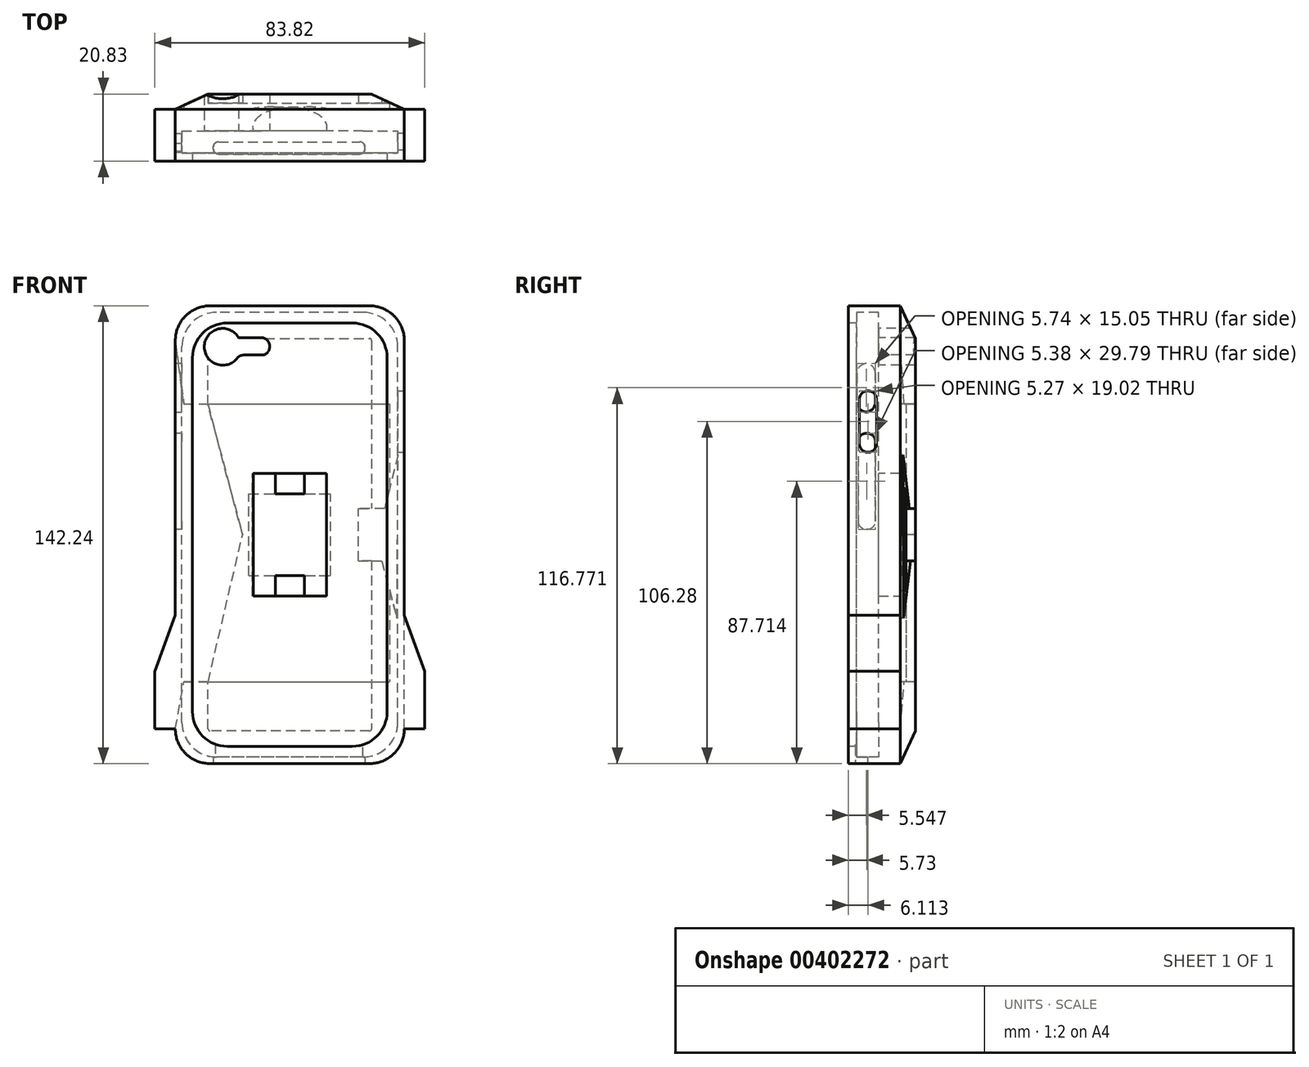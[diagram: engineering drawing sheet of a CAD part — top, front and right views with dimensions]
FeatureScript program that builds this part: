
annotation { "Feature Type Name" : "Feature", "Feature Type Description" : "" }
export const myFeature = defineFeature(function(context is Context, id is Id, definition is map)
    precondition{}
    {
        {
            var Q0;
            Q0=qCreatedBy(makeId("Front.planeOp"),FACE);
            var sketch = newSketch(context, id + "F0", { "sketchPlane" : qUnion([Q0])});
            skLineSegment(sketch, "E0.bottom", {"start": v(33.53, -69.09) * mm, "end": v(-33.53, -69.09) * mm});
            skLineSegment(sketch, "E0.top", {"start": v(33.53, 69.09) * mm, "end": v(-33.53, 69.09) * mm});
            skLineSegment(sketch, "E0.left", {"start": v(33.53, -69.09) * mm, "end": v(33.53, 69.09) * mm});
            skLineSegment(sketch, "E0.right", {"start": v(-33.53, -69.09) * mm, "end": v(-33.53, 69.09) * mm});
            skPoint(sketch, "E0.middle", {"position": v(0, 0) * mm});
            skSolve(sketch);
        }
        {
            var Q0;
            Q0=qCreatedBy(makeId("Front.planeOp"),FACE);
            var sketch = newSketch(context, id + "F1", { "sketchPlane" : qUnion([Q0])});
            skLineSegment(sketch, "E1.bottom", {"start": v(35.56, -71.12) * mm, "end": v(-35.56, -71.12) * mm});
            skLineSegment(sketch, "E1.top", {"start": v(35.56, 71.12) * mm, "end": v(-35.56, 71.12) * mm});
            skLineSegment(sketch, "E1.left", {"start": v(35.56, -71.12) * mm, "end": v(35.56, 71.12) * mm});
            skLineSegment(sketch, "E1.right", {"start": v(-35.56, -71.12) * mm, "end": v(-35.56, 71.12) * mm});
            skPoint(sketch, "E1.middle", {"position": v(0, 0) * mm});
            skSolve(sketch);
        }
        {
            var Q0;
            Q0=makeQuery(id+"F1.imprint","IMPRINT",FACE,{"disambiguationData":[TD([[makeQuery(id+"F1.imprint","IMPRINT",EDGE,{"derivedFrom":sQuery(id+"F1.wireOp",EDGE,"E1.bottom")}),-1.0]])]});
            extrude(context, id + "F2", {"entities" : qUnion([Q0]), "oppositeDirection" : true, "depth" : 11.94 * mm});
        }
        {
            var Q0;
            Q0=makeQuery(id+"F0.imprint","IMPRINT",FACE,{"disambiguationData":[TD([[makeQuery(id+"F0.imprint","IMPRINT",EDGE,{"derivedFrom":sQuery(id+"F0.wireOp",EDGE,"E0.bottom")}),-1.0]])]});
            extrude(context, id + "F3", {"entities" : qUnion([Q0]), "operationType" : NewBodyOperationType.REMOVE, "oppositeDirection" : true, "depth" : 9.4 * mm});
        }
        {
            var Q0;
            Q0=makeQuery(id+"F3.boolean.opBoolean","COPY",EDGE,{"derivedFrom":makeQuery(id+"F3.opExtrude","SWEPT_EDGE",EDGE,{"disambiguationData":[OSD([sQuery(id+"F0.wireOp",EDGE,"E0.top"),sQuery(id+"F0.wireOp",EDGE,"E0.right")])]})});
            var Q1;
            Q1=makeQuery(id+"F3.boolean.opBoolean","COPY",EDGE,{"derivedFrom":makeQuery(id+"F3.opExtrude","SWEPT_EDGE",EDGE,{"disambiguationData":[OSD([sQuery(id+"F0.wireOp",EDGE,"E0.top"),sQuery(id+"F0.wireOp",EDGE,"E0.left")])]})});
            var Q2;
            Q2=makeQuery(id+"F3.boolean.opBoolean","COPY",EDGE,{"derivedFrom":makeQuery(id+"F3.opExtrude","SWEPT_EDGE",EDGE,{"disambiguationData":[OSD([sQuery(id+"F0.wireOp",EDGE,"E0.bottom"),sQuery(id+"F0.wireOp",EDGE,"E0.left")])]})});
            var Q3;
            Q3=makeQuery(id+"F3.boolean.opBoolean","COPY",EDGE,{"derivedFrom":makeQuery(id+"F3.opExtrude","SWEPT_EDGE",EDGE,{"disambiguationData":[OSD([sQuery(id+"F0.wireOp",EDGE,"E0.bottom"),sQuery(id+"F0.wireOp",EDGE,"E0.right")])]})});
            fillet(context, id + "F4", {"entities" : qUnion([Q0, Q1, Q2, Q3]), "radius" : 10.8 * mm, "tangentPropagation" : true, "allowEdgeOverflow" : false});
        }
        {
            var Q0;
            Q0=makeQuery(id+"F2.opExtrude","SWEPT_EDGE",EDGE,{"disambiguationData":[OSD([sQuery(id+"F1.wireOp",EDGE,"E1.top"),sQuery(id+"F1.wireOp",EDGE,"E1.left")])]});
            var Q1;
            Q1=makeQuery(id+"F2.opExtrude","SWEPT_EDGE",EDGE,{"disambiguationData":[OSD([sQuery(id+"F1.wireOp",EDGE,"E1.top"),sQuery(id+"F1.wireOp",EDGE,"E1.right")])]});
            var Q2;
            Q2=makeQuery(id+"F2.opExtrude","SWEPT_EDGE",EDGE,{"disambiguationData":[OSD([sQuery(id+"F1.wireOp",EDGE,"E1.bottom"),sQuery(id+"F1.wireOp",EDGE,"E1.right")])]});
            var Q3;
            Q3=makeQuery(id+"F2.opExtrude","SWEPT_EDGE",EDGE,{"disambiguationData":[OSD([sQuery(id+"F1.wireOp",EDGE,"E1.bottom"),sQuery(id+"F1.wireOp",EDGE,"E1.left")])]});
            fillet(context, id + "F5", {"entities" : qUnion([Q0, Q1, Q2, Q3]), "radius" : 10.8 * mm, "tangentPropagation" : true, "allowEdgeOverflow" : false});
        }
        {
            var Q0;
            Q0=qCreatedBy(makeId("Right.planeOp"),FACE);
            var sketch = newSketch(context, id + "F6", { "sketchPlane" : qUnion([Q0])});
            skLineSegment(sketch, "E2.bottom", {"start": v(17.97, 40.7) * mm, "end": v(16.06, 40.7) * mm});
            skLineSegment(sketch, "E2.top", {"start": v(17.97, -45.67) * mm, "end": v(16.06, -45.67) * mm});
            skLineSegment(sketch, "E2.left", {"start": v(17.97, 40.7) * mm, "end": v(17.97, -45.67) * mm});
            skLineSegment(sketch, "E2.right", {"start": v(16.06, 40.7) * mm, "end": v(16.06, -45.67) * mm});
            skSolve(sketch);
        }
        {
            var Q0;
            Q0=qCreatedBy(makeId("Front.planeOp"),FACE);
            var sketch = newSketch(context, id + "F7", { "sketchPlane" : qUnion([Q0])});
            skLineSegment(sketch, "E3.bottom", {"start": v(33.53, -69.09) * mm, "end": v(-33.53, -69.09) * mm});
            skLineSegment(sketch, "E3.top", {"start": v(33.53, 69.09) * mm, "end": v(-33.53, 69.09) * mm});
            skLineSegment(sketch, "E3.left", {"start": v(33.53, -69.09) * mm, "end": v(33.53, 69.09) * mm});
            skLineSegment(sketch, "E3.right", {"start": v(-33.53, -69.09) * mm, "end": v(-33.53, 69.09) * mm});
            skPoint(sketch, "E3.middle", {"position": v(0, 0) * mm});
            skSolve(sketch);
        }
        {
            var Q0;
            Q0=qSketchRegion(id+"F7",true);
            extrude(context, id + "F8", {"entities" : qUnion([Q0]), "operationType" : NewBodyOperationType.ADD, "oppositeDirection" : true, "depth" : 2.54 * mm});
        }
        {
            var Q0;
            Q0=makeQuery(id+"F8.opExtrude","SWEPT_EDGE",EDGE,{"disambiguationData":[OSD([sQuery(id+"F7.wireOp",EDGE,"E3.top"),sQuery(id+"F7.wireOp",EDGE,"E3.right")])]});
            var Q1;
            Q1=makeQuery(id+"F8.opExtrude","SWEPT_EDGE",EDGE,{"disambiguationData":[OSD([sQuery(id+"F7.wireOp",EDGE,"E3.top"),sQuery(id+"F7.wireOp",EDGE,"E3.left")])]});
            var Q2;
            Q2=makeQuery(id+"F8.opExtrude","SWEPT_EDGE",EDGE,{"disambiguationData":[OSD([sQuery(id+"F7.wireOp",EDGE,"E3.bottom"),sQuery(id+"F7.wireOp",EDGE,"E3.left")])]});
            var Q3;
            Q3=makeQuery(id+"F8.opExtrude","SWEPT_EDGE",EDGE,{"disambiguationData":[OSD([sQuery(id+"F7.wireOp",EDGE,"E3.bottom"),sQuery(id+"F7.wireOp",EDGE,"E3.right")])]});
            fillet(context, id + "F9", {"entities" : qUnion([Q0, Q1, Q2, Q3]), "radius" : 10.8 * mm, "tangentPropagation" : true, "allowEdgeOverflow" : false});
        }
        {
            var Q0;
            Q0=qCreatedBy(makeId("Front.planeOp"),FACE);
            var sketch = newSketch(context, id + "F10", { "sketchPlane" : qUnion([Q0])});
            skLineSegment(sketch, "E4.bottom", {"start": v(30.23, -65.79) * mm, "end": v(-30.23, -65.79) * mm});
            skLineSegment(sketch, "E4.top", {"start": v(30.23, 65.79) * mm, "end": v(-30.23, 65.79) * mm});
            skLineSegment(sketch, "E4.left", {"start": v(30.23, -65.79) * mm, "end": v(30.23, 65.79) * mm});
            skLineSegment(sketch, "E4.right", {"start": v(-30.23, -65.79) * mm, "end": v(-30.23, 65.79) * mm});
            skPoint(sketch, "E4.middle", {"position": v(0, 0) * mm});
            skSolve(sketch);
        }
        {
            var Q0;
            Q0=makeQuery(id+"F10.imprint","IMPRINT",FACE,{"disambiguationData":[TD([[makeQuery(id+"F10.imprint","IMPRINT",EDGE,{"derivedFrom":sQuery(id+"F10.wireOp",EDGE,"E4.bottom")}),-1.0]])]});
            extrude(context, id + "F11", {"entities" : qUnion([Q0]), "operationType" : NewBodyOperationType.REMOVE, "oppositeDirection" : true, "depth" : 2.8 * mm});
        }
        {
            var Q0;
            Q0=makeQuery(id+"F11.boolean.opBoolean","COPY",EDGE,{"derivedFrom":makeQuery(id+"F11.opExtrude","SWEPT_EDGE",EDGE,{"disambiguationData":[OSD([sQuery(id+"F10.wireOp",EDGE,"E4.top"),sQuery(id+"F10.wireOp",EDGE,"E4.right")])]})});
            var Q1;
            Q1=makeQuery(id+"F11.boolean.opBoolean","COPY",EDGE,{"derivedFrom":makeQuery(id+"F11.opExtrude","SWEPT_EDGE",EDGE,{"disambiguationData":[OSD([sQuery(id+"F10.wireOp",EDGE,"E4.top"),sQuery(id+"F10.wireOp",EDGE,"E4.left")])]})});
            var Q2;
            Q2=makeQuery(id+"F11.boolean.opBoolean","COPY",EDGE,{"derivedFrom":makeQuery(id+"F11.opExtrude","SWEPT_EDGE",EDGE,{"disambiguationData":[OSD([sQuery(id+"F10.wireOp",EDGE,"E4.bottom"),sQuery(id+"F10.wireOp",EDGE,"E4.left")])]})});
            var Q3;
            Q3=makeQuery(id+"F11.boolean.opBoolean","COPY",EDGE,{"derivedFrom":makeQuery(id+"F11.opExtrude","SWEPT_EDGE",EDGE,{"disambiguationData":[OSD([sQuery(id+"F10.wireOp",EDGE,"E4.bottom"),sQuery(id+"F10.wireOp",EDGE,"E4.right")])]})});
            fillet(context, id + "F12", {"entities" : qUnion([Q0, Q1, Q2, Q3]), "radius" : 10.8 * mm, "tangentPropagation" : true, "allowEdgeOverflow" : false});
        }
        {
            var Q0;
            Q0=qCreatedBy(makeId("Right.planeOp"),FACE);
            var sketch = newSketch(context, id + "F13", { "sketchPlane" : qUnion([Q0])});
            skCircle(sketch, "E5", {"center": v(16.23, -1.76) * mm, "radius": 3.17 * mm});
            skSolve(sketch);
        }
        {
            var Q0;
            Q0=qSketchRegion(id+"F13",true);
            extrude(context, id + "F14", {"entities" : qUnion([Q0]), "operationType" : NewBodyOperationType.REMOVE, "endBound" : BoundingType.SYMMETRIC, "oppositeDirection" : true, "depth" : 101.6 * mm});
        }
        {
            var Q0;
            Q0=makeQuery(id+"F2.opExtrude","CAP_FACE",FACE,{"disambiguationData":[OSD([sQuery(id+"F1.wireOp",EDGE,"E1.bottom"),sQuery(id+"F1.wireOp",EDGE,"E1.top"),sQuery(id+"F1.wireOp",EDGE,"E1.left"),sQuery(id+"F1.wireOp",EDGE,"E1.right")])],"isStart":false});
            var sketch = newSketch(context, id + "F15", { "sketchPlane" : qUnion([Q0])});
            skLineSegment(sketch, "E6.bottom", {"start": v(35.56, -71.12) * mm, "end": v(-35.56, -71.12) * mm});
            skLineSegment(sketch, "E6.top", {"start": v(35.56, 71.12) * mm, "end": v(-35.56, 71.12) * mm});
            skLineSegment(sketch, "E6.left", {"start": v(35.56, -71.12) * mm, "end": v(35.56, 71.12) * mm});
            skLineSegment(sketch, "E6.right", {"start": v(-35.56, -71.12) * mm, "end": v(-35.56, 71.12) * mm});
            skPoint(sketch, "E6.middle", {"position": v(0, 0) * mm});
            skSolve(sketch);
        }
        {
            var Q0;
            Q0 = qSketchRegion(id + "F15", true);
            extrude(context, id + "F16", {"entities" : qUnion([Q0]), "operationType" : NewBodyOperationType.ADD, "depth" : 8.9 * mm});
        }
        {
            var Q0;
            Q0=makeQuery(id+"F16.opExtrude","SWEPT_EDGE",EDGE,{"disambiguationData":[OSD([sQuery(id+"F15.wireOp",EDGE,"E6.top"),sQuery(id+"F15.wireOp",EDGE,"E6.left")])]});
            var Q1;
            Q1=makeQuery(id+"F16.opExtrude","SWEPT_EDGE",EDGE,{"disambiguationData":[OSD([sQuery(id+"F15.wireOp",EDGE,"E6.top"),sQuery(id+"F15.wireOp",EDGE,"E6.right")])]});
            var Q2;
            Q2=makeQuery(id+"F16.opExtrude","SWEPT_EDGE",EDGE,{"disambiguationData":[OSD([sQuery(id+"F15.wireOp",EDGE,"E6.bottom"),sQuery(id+"F15.wireOp",EDGE,"E6.right")])]});
            var Q3;
            Q3=makeQuery(id+"F16.opExtrude","SWEPT_EDGE",EDGE,{"disambiguationData":[OSD([sQuery(id+"F15.wireOp",EDGE,"E6.bottom"),sQuery(id+"F15.wireOp",EDGE,"E6.left")])]});
            fillet(context, id + "F17", {"entities" : qUnion([Q0, Q1, Q2, Q3]), "radius" : 10.8 * mm, "tangentPropagation" : true, "allowEdgeOverflow" : false});
        }
        {
            var Q0;
            Q0 = qSketchRegion(id + "F6", true);
            extrude(context, id + "F18", {"entities" : qUnion([Q0]), "operationType" : NewBodyOperationType.REMOVE, "oppositeDirection" : true, "depth" : 45.97 * mm});
        }
        {
            var Q0;
            Q0=makeQuery(id+"F16.opExtrude","CAP_EDGE",EDGE,{"disambiguationData":[OSD([sQuery(id+"F15.wireOp",EDGE,"E6.left")])],"isStart":false});
            var Q1;
            Q1=makeQuery(id+"F16.opExtrude","CAP_EDGE",EDGE,{"disambiguationData":[OSD([sQuery(id+"F15.wireOp",EDGE,"E6.right")])],"isStart":false});
            chamfer(context, id + "F19", {"entities" : qUnion([Q0, Q1]), "chamferType" : ChamferType.OFFSET_ANGLE, "width" : 10.16 * mm, "oppositeDirection" : false, "angle" : 25 * degree, "tangentPropagation" : true});
        }
        {
            var Q0;
            Q0=makeQuery(id+"F18.boolean.opBoolean","COPY",FACE,{"derivedFrom":makeQuery(id+"F18.opExtrude","SWEPT_FACE",FACE,{"disambiguationData":[OSD([sQuery(id+"F6.wireOp",EDGE,"E2.right")])]})});
            var sketch = newSketch(context, id + "F20", { "sketchPlane" : qUnion([Q0])});
            skLineSegment(sketch, "E7", {"start": v(35.56, 60.36) * mm, "end": v(32.88, 40.7) * mm});
            skLineSegment(sketch, "E8", {"start": v(32.88, 40.7) * mm, "end": v(25.49, 40.7) * mm});
            skLineSegment(sketch, "E9", {"start": v(25.49, 40.7) * mm, "end": v(14.68, 0) * mm});
            skLineSegment(sketch, "E10", {"start": v(14.68, 0) * mm, "end": v(25.36, -45.67) * mm});
            skLineSegment(sketch, "E11", {"start": v(25.36, -45.67) * mm, "end": v(32.88, -45.67) * mm});
            skLineSegment(sketch, "E12", {"start": v(32.88, -45.67) * mm, "end": v(35.56, -60.32) * mm});
            skLineSegment(sketch, "E13", {"start": v(35.56, -60.32) * mm, "end": v(35.56, 60.36) * mm});
            skSolve(sketch);
        }
        {
            var Q0;
            Q0 = qSketchRegion(id + "F20", true);
            extrude(context, id + "F21", {"entities" : qUnion([Q0]), "operationType" : NewBodyOperationType.REMOVE, "depth" : 45.47 * mm});
        }
        {
            var Q0;
            Q0=makeQuery(id+"F21.boolean.opBoolean","MERGE",FACE,{"derivedFrom":[makeQuery(id+"F18.boolean.opBoolean","COPY",FACE,{"derivedFrom":makeQuery(id+"F18.opExtrude","SWEPT_FACE",FACE,{"disambiguationData":[OSD([sQuery(id+"F6.wireOp",EDGE,"E2.right")])]})}),makeQuery(id+"F21.opExtrude","CAP_FACE",FACE,{"disambiguationData":[OSD([sQuery(id+"F20.wireOp",EDGE,"E7"),sQuery(id+"F20.wireOp",EDGE,"E8"),sQuery(id+"F20.wireOp",EDGE,"E9"),sQuery(id+"F20.wireOp",EDGE,"E10"),sQuery(id+"F20.wireOp",EDGE,"E11"),sQuery(id+"F20.wireOp",EDGE,"E12"),sQuery(id+"F20.wireOp",EDGE,"E13")])],"isStart":true})]});
            var sketch = newSketch(context, id + "F22", { "sketchPlane" : qUnion([Q0])});
            skLineSegment(sketch, "E14", {"start": v(-33.6, 24.75) * mm, "end": v(-29.43, 8.07) * mm});
            skLineSegment(sketch, "E15", {"start": v(-29.43, 8.07) * mm, "end": v(-21.34, 8.07) * mm});
            skLineSegment(sketch, "E16", {"start": v(-21.34, 8.07) * mm, "end": v(-21.34, -8.12) * mm});
            skLineSegment(sketch, "E17", {"start": v(-21.34, -8.12) * mm, "end": v(-28.55, -8.12) * mm});
            skLineSegment(sketch, "E18", {"start": v(-28.55, -8.12) * mm, "end": v(-33.26, -25.98) * mm});
            skLineSegment(sketch, "E19", {"start": v(-33.26, -25.98) * mm, "end": v(-33.6, 24.75) * mm});
            skSolve(sketch);
        }
        {
            var Q0;
            Q0 = qSketchRegion(id + "F22", true);
            extrude(context, id + "F23", {"entities" : qUnion([Q0]), "operationType" : NewBodyOperationType.REMOVE, "depth" : 84.58 * mm});
        }
        {
            var Q0;
            Q0 = qSketchRegion(id + "F6", true);
            extrude(context, id + "F24", {"entities" : qUnion([Q0]), "operationType" : NewBodyOperationType.REMOVE, "depth" : 30.99 * mm});
        }
        {
            var Q0;
            Q0=makeQuery(id+"F16.boolean.opBoolean","MERGE",FACE,{"derivedFrom":[makeQuery(id+"F2.opExtrude","SWEPT_FACE",FACE,{"disambiguationData":[OSD([sQuery(id+"F1.wireOp",EDGE,"E1.left")])]}),makeQuery(id+"F16.opExtrude","SWEPT_FACE",FACE,{"disambiguationData":[OSD([sQuery(id+"F15.wireOp",EDGE,"E6.right")])]})]});
            var sketch = newSketch(context, id + "F25", { "sketchPlane" : qUnion([Q0])});
            skLineSegment(sketch, "E20.bottom", {"start": v(3.48, 44.67) * mm, "end": v(8.75, 44.67) * mm});
            skLineSegment(sketch, "E20.top", {"start": v(3.48, 25.65) * mm, "end": v(8.75, 25.65) * mm});
            skLineSegment(sketch, "E20.left", {"start": v(3.48, 44.67) * mm, "end": v(3.48, 25.65) * mm});
            skLineSegment(sketch, "E20.right", {"start": v(8.75, 44.67) * mm, "end": v(8.75, 25.65) * mm});
            skSolve(sketch);
        }
        {
            var Q0;
            Q0=makeQuery(id+"F25.imprint","IMPRINT",FACE,{"disambiguationData":[TD([[makeQuery(id+"F25.imprint","IMPRINT",EDGE,{"derivedFrom":sQuery(id+"F25.wireOp",EDGE,"E20.bottom")}),-1.0]])]});
            extrude(context, id + "F26", {"entities" : qUnion([Q0]), "operationType" : NewBodyOperationType.REMOVE, "oppositeDirection" : true, "depth" : 9.65 * mm});
        }
        {
            var Q0;
            Q0=makeQuery(id+"F26.boolean.opBoolean","COPY",EDGE,{"derivedFrom":makeQuery(id+"F26.opExtrude","SWEPT_EDGE",EDGE,{"disambiguationData":[OSD([sQuery(id+"F25.wireOp",EDGE,"E20.bottom"),sQuery(id+"F25.wireOp",EDGE,"E20.right")])]})});
            var Q1;
            Q1=makeQuery(id+"F26.boolean.opBoolean","COPY",EDGE,{"derivedFrom":makeQuery(id+"F26.opExtrude","SWEPT_EDGE",EDGE,{"disambiguationData":[OSD([sQuery(id+"F25.wireOp",EDGE,"E20.bottom"),sQuery(id+"F25.wireOp",EDGE,"E20.left")])]})});
            var Q2;
            Q2=makeQuery(id+"F26.boolean.opBoolean","COPY",EDGE,{"derivedFrom":makeQuery(id+"F26.opExtrude","SWEPT_EDGE",EDGE,{"disambiguationData":[OSD([sQuery(id+"F25.wireOp",EDGE,"E20.top"),sQuery(id+"F25.wireOp",EDGE,"E20.right")])]})});
            var Q3;
            Q3=makeQuery(id+"F26.boolean.opBoolean","COPY",EDGE,{"derivedFrom":makeQuery(id+"F26.opExtrude","SWEPT_EDGE",EDGE,{"disambiguationData":[OSD([sQuery(id+"F25.wireOp",EDGE,"E20.top"),sQuery(id+"F25.wireOp",EDGE,"E20.left")])]})});
            fillet(context, id + "F27", {"entities" : qUnion([Q0, Q1, Q2, Q3]), "radius" : 2.45 * mm, "tangentPropagation" : true, "allowEdgeOverflow" : false});
        }
        {
            var Q0;
            Q0=makeQuery(id+"F3.boolean.opBoolean","COPY",FACE,{"derivedFrom":makeQuery(id+"F3.opExtrude","CAP_FACE",FACE,{"disambiguationData":[OSD([sQuery(id+"F0.wireOp",EDGE,"E0.bottom"),sQuery(id+"F0.wireOp",EDGE,"E0.top"),sQuery(id+"F0.wireOp",EDGE,"E0.left"),sQuery(id+"F0.wireOp",EDGE,"E0.right")])],"isStart":false})});
            var sketch = newSketch(context, id + "F28", { "sketchPlane" : qUnion([Q0])});
            skCircle(sketch, "E21", {"center": v(-20.85, 58.37) * mm, "radius": 5.72 * mm});
            skSolve(sketch);
        }
        {
            var Q0;
            Q0=makeQuery(id+"F28.imprint","IMPRINT",FACE,{"disambiguationData":[TD([[makeQuery(id+"F28.imprint","IMPRINT",EDGE,{"derivedFrom":sQuery(id+"F28.wireOp",EDGE,"E21")}),1.0]])]});
            extrude(context, id + "F29", {"entities" : qUnion([Q0]), "operationType" : NewBodyOperationType.REMOVE, "oppositeDirection" : true, "depth" : 25.4 * mm});
        }
        {
            var Q0;
            Q0=makeQuery(id+"F3.boolean.opBoolean","COPY",FACE,{"derivedFrom":makeQuery(id+"F3.opExtrude","CAP_FACE",FACE,{"disambiguationData":[OSD([sQuery(id+"F0.wireOp",EDGE,"E0.bottom"),sQuery(id+"F0.wireOp",EDGE,"E0.top"),sQuery(id+"F0.wireOp",EDGE,"E0.left"),sQuery(id+"F0.wireOp",EDGE,"E0.right")])],"isStart":false})});
            var sketch = newSketch(context, id + "F30", { "sketchPlane" : qUnion([Q0])});
            skLineSegment(sketch, "E22.bottom", {"start": v(-20.56, 55.8) * mm, "end": v(-6.28, 55.8) * mm});
            skLineSegment(sketch, "E22.top", {"start": v(-20.56, 61.2) * mm, "end": v(-6.28, 61.2) * mm});
            skLineSegment(sketch, "E22.left", {"start": v(-20.56, 55.8) * mm, "end": v(-20.56, 61.2) * mm});
            skLineSegment(sketch, "E22.right", {"start": v(-6.28, 55.8) * mm, "end": v(-6.28, 61.2) * mm});
            skSolve(sketch);
        }
        {
            var Q0;
            Q0 = qSketchRegion(id + "F30", true);
            extrude(context, id + "F31", {"entities" : qUnion([Q0]), "operationType" : NewBodyOperationType.REMOVE, "oppositeDirection" : true, "depth" : 25.4 * mm});
        }
        {
            var Q0;
            Q0=makeQuery(id+"F31.boolean.opBoolean","COPY",EDGE,{"derivedFrom":makeQuery(id+"F31.opExtrude","SWEPT_EDGE",EDGE,{"disambiguationData":[OSD([sQuery(id+"F30.wireOp",EDGE,"E22.top"),sQuery(id+"F30.wireOp",EDGE,"E22.right")])]})});
            var Q1;
            Q1=makeQuery(id+"F31.boolean.opBoolean","COPY",EDGE,{"derivedFrom":makeQuery(id+"F31.opExtrude","SWEPT_EDGE",EDGE,{"disambiguationData":[OSD([sQuery(id+"F30.wireOp",EDGE,"E22.bottom"),sQuery(id+"F30.wireOp",EDGE,"E22.right")])]})});
            var Q2;
            Q2=makeQuery(id+"F31.boolean.opBoolean","INTERSECT",EDGE,{"derivedFrom":[makeQuery(id+"F29.boolean.opBoolean","COPY",FACE,{"derivedFrom":makeQuery(id+"F29.opExtrude","SWEPT_FACE",FACE,{"disambiguationData":[OSD([sQuery(id+"F28.wireOp",EDGE,"E21")])]})}),makeQuery(id+"F31.opExtrude","SWEPT_FACE",FACE,{"disambiguationData":[OSD([sQuery(id+"F30.wireOp",EDGE,"E22.bottom")])]})]});
            fillet(context, id + "F32", {"entities" : qUnion([Q0, Q1, Q2]), "radius" : 2.47 * mm, "tangentPropagation" : true, "allowEdgeOverflow" : false});
        }
        {
            var Q0;
            {var subQ0=sQuery(id+"F6.wireOp",EDGE,"E2.right");Q0=makeQuery(id+"F24.boolean.opBoolean","MERGE",FACE,{"derivedFrom":[makeQuery(id+"F21.boolean.opBoolean","MERGE",FACE,{"derivedFrom":[makeQuery(id+"F18.boolean.opBoolean","COPY",FACE,{"derivedFrom":makeQuery(id+"F18.opExtrude","SWEPT_FACE",FACE,{"disambiguationData":[OSD([subQ0])]})}),makeQuery(id+"F21.opExtrude","CAP_FACE",FACE,{"disambiguationData":[OSD([sQuery(id+"F20.wireOp",EDGE,"E7"),sQuery(id+"F20.wireOp",EDGE,"E8"),sQuery(id+"F20.wireOp",EDGE,"E9"),sQuery(id+"F20.wireOp",EDGE,"E10"),sQuery(id+"F20.wireOp",EDGE,"E11"),sQuery(id+"F20.wireOp",EDGE,"E12"),sQuery(id+"F20.wireOp",EDGE,"E13")])],"isStart":true})]}),makeQuery(id+"F23.boolean.opBoolean","COPY",FACE,{"derivedFrom":makeQuery(id+"F23.opExtrude","CAP_FACE",FACE,{"disambiguationData":[OSD([sQuery(id+"F22.wireOp",EDGE,"E14"),sQuery(id+"F22.wireOp",EDGE,"E15"),sQuery(id+"F22.wireOp",EDGE,"E16"),sQuery(id+"F22.wireOp",EDGE,"E17"),sQuery(id+"F22.wireOp",EDGE,"E18"),sQuery(id+"F22.wireOp",EDGE,"E19")])],"isStart":true})}),makeQuery(id+"F24.opExtrude","SWEPT_FACE",FACE,{"disambiguationData":[OSD([subQ0])]})]});}
            var sketch = newSketch(context, id + "F33", { "sketchPlane" : qUnion([Q0])});
            skLineSegment(sketch, "E23.bottom", {"start": v(12.7, -12.7) * mm, "end": v(-12.7, -12.7) * mm});
            skLineSegment(sketch, "E23.top", {"start": v(12.7, 12.7) * mm, "end": v(-12.7, 12.7) * mm});
            skLineSegment(sketch, "E23.left", {"start": v(12.7, -12.7) * mm, "end": v(12.7, 12.7) * mm});
            skLineSegment(sketch, "E23.right", {"start": v(-12.7, -12.7) * mm, "end": v(-12.7, 12.7) * mm});
            skPoint(sketch, "E23.middle", {"position": v(0, 0) * mm});
            skSolve(sketch);
        }
        {
            var Q0;
            Q0 = qSketchRegion(id + "F33", true);
            extrude(context, id + "F34", {"entities" : qUnion([Q0]), "operationType" : NewBodyOperationType.ADD, "depth" : 0.76 * mm});
        }
        {
            var Q0;
            Q0=qCreatedBy(makeId("Top.planeOp"),FACE);
            var sketch = newSketch(context, id + "F35", { "sketchPlane" : qUnion([Q0])});
            skEllipse(sketch, "E24", {"center": v(0, 10.46) * mm, "majorRadius": 11.54 * mm, "minorRadius": 6.09 * mm, "majorAxis": v(-1, 0)});
            skSolve(sketch);
        }
        {
            var Q0;
            Q0 = qSketchRegion(id + "F35", true);
            extrude(context, id + "F36", {"entities" : qUnion([Q0]), "operationType" : NewBodyOperationType.REMOVE, "endBound" : BoundingType.SYMMETRIC, "oppositeDirection" : true, "depth" : 38.1 * mm});
        }
        {
            var Q0;
            Q0=makeQuery(id+"F34.opExtrude","CAP_EDGE",EDGE,{"disambiguationData":[OSD([sQuery(id+"F33.wireOp",EDGE,"E23.left")])],"isStart":false});
            var Q1;
            Q1=makeQuery(id+"F34.opExtrude","CAP_EDGE",EDGE,{"disambiguationData":[OSD([sQuery(id+"F33.wireOp",EDGE,"E23.right")])],"isStart":false});
            fillet(context, id + "F37", {"entities" : qUnion([Q0, Q1]), "radius" : 39.92 * mm, "tangentPropagation" : true, "allowEdgeOverflow" : false});
        }
        {
            var Q0;
            Q0=makeQuery(id+"F16.boolean.opBoolean","MERGE",FACE,{"derivedFrom":[makeQuery(id+"F2.opExtrude","SWEPT_FACE",FACE,{"disambiguationData":[OSD([sQuery(id+"F1.wireOp",EDGE,"E1.bottom")])]}),makeQuery(id+"F16.opExtrude","SWEPT_FACE",FACE,{"disambiguationData":[OSD([sQuery(id+"F15.wireOp",EDGE,"E6.bottom")])]})]});
            var sketch = newSketch(context, id + "F38", { "sketchPlane" : qUnion([Q0])});
            skPoint(sketch, "E25.oppositeSnap0", {"position": v(24.76, -5.97) * mm});
            skLineSegment(sketch, "E25.bottom", {"start": v(-23.73, -2.16) * mm, "end": v(23.28, -2.16) * mm});
            skLineSegment(sketch, "E25.top", {"start": v(-23.73, -5.97) * mm, "end": v(23.28, -5.97) * mm});
            skLineSegment(sketch, "E25.left", {"start": v(-23.73, -2.16) * mm, "end": v(-23.73, -5.97) * mm});
            skLineSegment(sketch, "E25.right", {"start": v(23.28, -2.16) * mm, "end": v(23.28, -5.97) * mm});
            skSolve(sketch);
        }
        {
            var Q0;
            Q0=makeQuery(id+"F38.imprint","IMPRINT",FACE,{"disambiguationData":[TD([[makeQuery(id+"F38.imprint","IMPRINT",EDGE,{"derivedFrom":sQuery(id+"F38.wireOp",EDGE,"E25.bottom")}),-1.0]])]});
            extrude(context, id + "F39", {"entities" : qUnion([Q0]), "operationType" : NewBodyOperationType.REMOVE, "oppositeDirection" : true, "depth" : 25.4 * mm});
        }
        {
            var Q0;
            Q0=makeQuery(id+"F39.boolean.opBoolean","COPY",EDGE,{"derivedFrom":makeQuery(id+"F39.opExtrude","SWEPT_EDGE",EDGE,{"disambiguationData":[OSD([sQuery(id+"F38.wireOp",EDGE,"E25.top"),sQuery(id+"F38.wireOp",EDGE,"E25.left")])]})});
            var Q1;
            Q1=makeQuery(id+"F39.boolean.opBoolean","COPY",EDGE,{"derivedFrom":makeQuery(id+"F39.opExtrude","SWEPT_EDGE",EDGE,{"disambiguationData":[OSD([sQuery(id+"F38.wireOp",EDGE,"E25.bottom"),sQuery(id+"F38.wireOp",EDGE,"E25.left")])]})});
            var Q2;
            Q2=makeQuery(id+"F39.boolean.opBoolean","COPY",EDGE,{"derivedFrom":makeQuery(id+"F39.opExtrude","SWEPT_EDGE",EDGE,{"disambiguationData":[OSD([sQuery(id+"F38.wireOp",EDGE,"E25.bottom"),sQuery(id+"F38.wireOp",EDGE,"E25.right")])]})});
            var Q3;
            Q3=makeQuery(id+"F39.boolean.opBoolean","COPY",EDGE,{"derivedFrom":makeQuery(id+"F39.opExtrude","SWEPT_EDGE",EDGE,{"disambiguationData":[OSD([sQuery(id+"F38.wireOp",EDGE,"E25.top"),sQuery(id+"F38.wireOp",EDGE,"E25.right")])]})});
            fillet(context, id + "F40", {"entities" : qUnion([Q0, Q1, Q2, Q3]), "radius" : 1.6 * mm, "tangentPropagation" : true, "allowEdgeOverflow" : false});
        }
        {
            var Q0;
            Q0=makeQuery(id+"F16.boolean.opBoolean","MERGE",FACE,{"derivedFrom":[makeQuery(id+"F2.opExtrude","SWEPT_FACE",FACE,{"disambiguationData":[OSD([sQuery(id+"F1.wireOp",EDGE,"E1.right")])]}),makeQuery(id+"F16.opExtrude","SWEPT_FACE",FACE,{"disambiguationData":[OSD([sQuery(id+"F15.wireOp",EDGE,"E6.left")])]})]});
            var sketch = newSketch(context, id + "F41", { "sketchPlane" : qUnion([Q0])});
            skLineSegment(sketch, "E26.bottom", {"start": v(-8.42, 53.18) * mm, "end": v(-2.67, 53.18) * mm});
            skLineSegment(sketch, "E26.top", {"start": v(-8.42, 38.12) * mm, "end": v(-2.67, 38.12) * mm});
            skLineSegment(sketch, "E26.left", {"start": v(-8.42, 53.18) * mm, "end": v(-8.42, 38.12) * mm});
            skLineSegment(sketch, "E26.right", {"start": v(-2.67, 53.18) * mm, "end": v(-2.67, 38.12) * mm});
            skSolve(sketch);
        }
        {
            var Q0;
            Q0=makeQuery(id+"F41.imprint","IMPRINT",FACE,{"disambiguationData":[TD([[makeQuery(id+"F41.imprint","IMPRINT",EDGE,{"derivedFrom":sQuery(id+"F41.wireOp",EDGE,"E26.bottom")}),-1.0]])]});
            extrude(context, id + "F42", {"entities" : qUnion([Q0]), "operationType" : NewBodyOperationType.REMOVE, "oppositeDirection" : true, "depth" : 25.4 * mm});
        }
        {
            var Q0;
            Q0=makeQuery(id+"F42.boolean.opBoolean","COPY",EDGE,{"derivedFrom":makeQuery(id+"F42.opExtrude","SWEPT_EDGE",EDGE,{"disambiguationData":[OSD([sQuery(id+"F41.wireOp",EDGE,"E26.bottom"),sQuery(id+"F41.wireOp",EDGE,"E26.left")])]})});
            var Q1;
            Q1=makeQuery(id+"F42.boolean.opBoolean","COPY",EDGE,{"derivedFrom":makeQuery(id+"F42.opExtrude","SWEPT_EDGE",EDGE,{"disambiguationData":[OSD([sQuery(id+"F41.wireOp",EDGE,"E26.bottom"),sQuery(id+"F41.wireOp",EDGE,"E26.right")])]})});
            var Q2;
            Q2=makeQuery(id+"F42.boolean.opBoolean","COPY",EDGE,{"derivedFrom":makeQuery(id+"F42.opExtrude","SWEPT_EDGE",EDGE,{"disambiguationData":[OSD([sQuery(id+"F41.wireOp",EDGE,"E26.top"),sQuery(id+"F41.wireOp",EDGE,"E26.left")])]})});
            var Q3;
            Q3=makeQuery(id+"F42.boolean.opBoolean","COPY",EDGE,{"derivedFrom":makeQuery(id+"F42.opExtrude","SWEPT_EDGE",EDGE,{"disambiguationData":[OSD([sQuery(id+"F41.wireOp",EDGE,"E26.top"),sQuery(id+"F41.wireOp",EDGE,"E26.right")])]})});
            fillet(context, id + "F43", {"entities" : qUnion([Q0, Q1, Q2, Q3]), "radius" : 3.07 * mm, "tangentPropagation" : true, "allowEdgeOverflow" : false});
        }
        {
            var Q0;
            Q0=makeQuery(id+"F16.boolean.opBoolean","MERGE",FACE,{"derivedFrom":[makeQuery(id+"F2.opExtrude","SWEPT_FACE",FACE,{"disambiguationData":[OSD([sQuery(id+"F1.wireOp",EDGE,"E1.right")])]}),makeQuery(id+"F16.opExtrude","SWEPT_FACE",FACE,{"disambiguationData":[OSD([sQuery(id+"F15.wireOp",EDGE,"E6.left")])]})]});
            var sketch = newSketch(context, id + "F44", { "sketchPlane" : qUnion([Q0])});
            skLineSegment(sketch, "E27.bottom", {"start": v(-8.42, 31.49) * mm, "end": v(-3.04, 31.49) * mm});
            skLineSegment(sketch, "E27.top", {"start": v(-8.42, 1.7) * mm, "end": v(-3.04, 1.7) * mm});
            skLineSegment(sketch, "E27.left", {"start": v(-8.42, 31.49) * mm, "end": v(-8.42, 1.7) * mm});
            skLineSegment(sketch, "E27.right", {"start": v(-3.04, 31.49) * mm, "end": v(-3.04, 1.7) * mm});
            skSolve(sketch);
        }
        {
            var Q0;
            Q0=makeQuery(id+"F44.imprint","IMPRINT",FACE,{"disambiguationData":[TD([[makeQuery(id+"F44.imprint","IMPRINT",EDGE,{"derivedFrom":sQuery(id+"F44.wireOp",EDGE,"E27.bottom")}),-1.0]])]});
            extrude(context, id + "F45", {"entities" : qUnion([Q0]), "operationType" : NewBodyOperationType.REMOVE, "oppositeDirection" : true, "depth" : 25.4 * mm});
        }
        {
            var Q0;
            Q0=makeQuery(id+"F45.boolean.opBoolean","COPY",EDGE,{"derivedFrom":makeQuery(id+"F45.opExtrude","SWEPT_EDGE",EDGE,{"disambiguationData":[OSD([sQuery(id+"F44.wireOp",EDGE,"E27.bottom"),sQuery(id+"F44.wireOp",EDGE,"E27.left")])]})});
            var Q1;
            Q1=makeQuery(id+"F45.boolean.opBoolean","COPY",EDGE,{"derivedFrom":makeQuery(id+"F45.opExtrude","SWEPT_EDGE",EDGE,{"disambiguationData":[OSD([sQuery(id+"F44.wireOp",EDGE,"E27.bottom"),sQuery(id+"F44.wireOp",EDGE,"E27.right")])]})});
            var Q2;
            Q2=makeQuery(id+"F45.boolean.opBoolean","COPY",EDGE,{"derivedFrom":makeQuery(id+"F45.opExtrude","SWEPT_EDGE",EDGE,{"disambiguationData":[OSD([sQuery(id+"F44.wireOp",EDGE,"E27.top"),sQuery(id+"F44.wireOp",EDGE,"E27.left")])]})});
            var Q3;
            Q3=makeQuery(id+"F45.boolean.opBoolean","COPY",EDGE,{"derivedFrom":makeQuery(id+"F45.opExtrude","SWEPT_EDGE",EDGE,{"disambiguationData":[OSD([sQuery(id+"F44.wireOp",EDGE,"E27.top"),sQuery(id+"F44.wireOp",EDGE,"E27.right")])]})});
            fillet(context, id + "F46", {"entities" : qUnion([Q0, Q1, Q2, Q3]), "radius" : 2.5 * mm, "tangentPropagation" : true, "allowEdgeOverflow" : false});
        }
        {
            var Q0;
            Q0=makeQuery(id+"F16.boolean.opBoolean","MERGE",FACE,{"derivedFrom":[makeQuery(id+"F2.opExtrude","SWEPT_FACE",FACE,{"disambiguationData":[OSD([sQuery(id+"F1.wireOp",EDGE,"E1.right")])]}),makeQuery(id+"F16.opExtrude","SWEPT_FACE",FACE,{"disambiguationData":[OSD([sQuery(id+"F15.wireOp",EDGE,"E6.left")])]})]});
            var sketch = newSketch(context, id + "F47", { "sketchPlane" : qUnion([Q0])});
            skLineSegment(sketch, "E28.bottom", {"start": v(-16.06, -60.32) * mm, "end": v(0, -60.32) * mm});
            skLineSegment(sketch, "E28.top", {"start": v(-16.06, -14.6) * mm, "end": v(0, -14.6) * mm});
            skLineSegment(sketch, "E28.left", {"start": v(-16.06, -60.32) * mm, "end": v(-16.06, -14.6) * mm});
            skLineSegment(sketch, "E28.right", {"start": v(0, -60.32) * mm, "end": v(0, -14.6) * mm});
            skSolve(sketch);
        }
        {
            var Q0;
            Q0=makeQuery(id+"F47.imprint","IMPRINT",FACE,{"disambiguationData":[TD([[makeQuery(id+"F47.imprint","IMPRINT",EDGE,{"derivedFrom":sQuery(id+"F47.wireOp",EDGE,"E28.bottom")}),1.0]])]});
            extrude(context, id + "F48", {"entities" : qUnion([Q0]), "operationType" : NewBodyOperationType.ADD, "depth" : 6.35 * mm});
        }
        {
            var Q0;
            Q0=makeQuery(id+"F48.opExtrude","CAP_EDGE",EDGE,{"disambiguationData":[OSD([sQuery(id+"F47.wireOp",EDGE,"E28.top")])],"isStart":false});
            chamfer(context, id + "F49", {"entities" : qUnion([Q0]), "chamferType" : ChamferType.OFFSET_ANGLE, "width" : 10.16 * mm, "oppositeDirection" : false, "angle" : 70 * degree, "tangentPropagation" : true});
        }
        {
            var Q0;
            Q0=makeQuery(id+"F16.boolean.opBoolean","MERGE",FACE,{"derivedFrom":[makeQuery(id+"F2.opExtrude","SWEPT_FACE",FACE,{"disambiguationData":[OSD([sQuery(id+"F1.wireOp",EDGE,"E1.left")])]}),makeQuery(id+"F16.opExtrude","SWEPT_FACE",FACE,{"disambiguationData":[OSD([sQuery(id+"F15.wireOp",EDGE,"E6.right")])]})]});
            var sketch = newSketch(context, id + "F50", { "sketchPlane" : qUnion([Q0])});
            skLineSegment(sketch, "E29.bottom", {"start": v(0, -60.33) * mm, "end": v(16.1, -60.33) * mm});
            skLineSegment(sketch, "E29.top", {"start": v(0, -14.56) * mm, "end": v(16.1, -14.56) * mm});
            skLineSegment(sketch, "E29.left", {"start": v(0, -60.33) * mm, "end": v(0, -14.56) * mm});
            skLineSegment(sketch, "E29.right", {"start": v(16.1, -60.33) * mm, "end": v(16.1, -14.56) * mm});
            skSolve(sketch);
        }
        {
            var Q0;
            Q0=makeQuery(id+"F50.imprint","IMPRINT",FACE,{"disambiguationData":[TD([[makeQuery(id+"F50.imprint","IMPRINT",EDGE,{"derivedFrom":sQuery(id+"F50.wireOp",EDGE,"E29.top")}),-1.0]])]});
            extrude(context, id + "F51", {"entities" : qUnion([Q0]), "operationType" : NewBodyOperationType.ADD, "depth" : 6.35 * mm});
        }
        {
            var Q0;
            Q0=makeQuery(id+"F51.opExtrude","CAP_EDGE",EDGE,{"disambiguationData":[OSD([sQuery(id+"F50.wireOp",EDGE,"E29.top")])],"isStart":false});
            chamfer(context, id + "F52", {"entities" : qUnion([Q0]), "chamferType" : ChamferType.OFFSET_ANGLE, "width" : 10.16 * mm, "oppositeDirection" : false, "angle" : 70 * degree, "tangentPropagation" : true});
        }
    });
